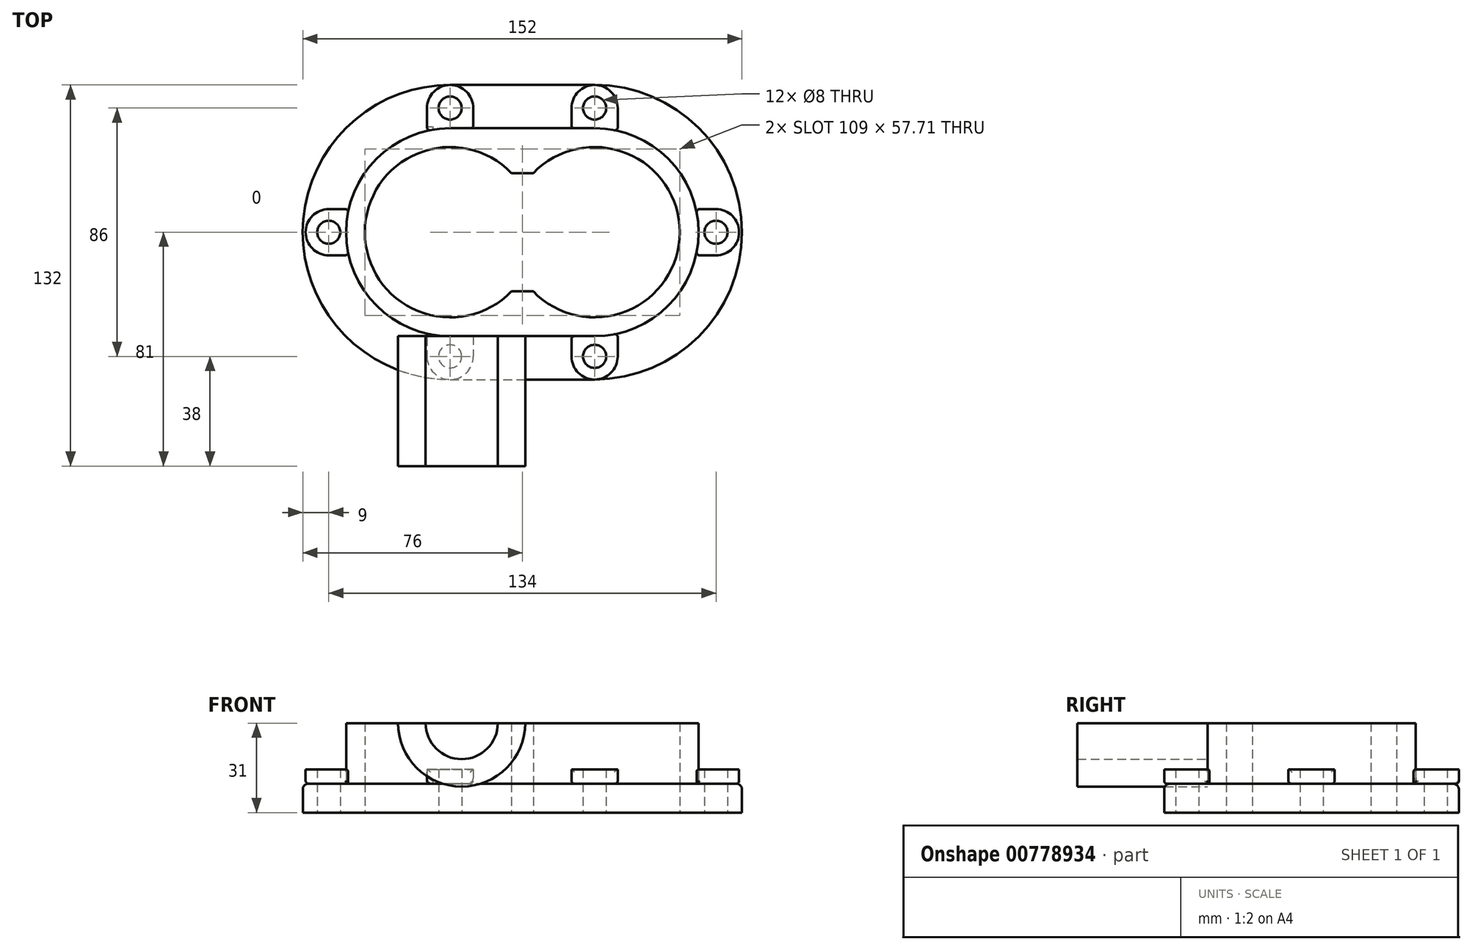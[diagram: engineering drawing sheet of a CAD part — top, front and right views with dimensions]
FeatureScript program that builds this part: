
annotation { "Feature Type Name" : "Feature", "Feature Type Description" : "" }
export const myFeature = defineFeature(function(context is Context, id is Id, definition is map)
    precondition{}
    {
        {
            var Q0;
            Q0=qCreatedBy(makeId("Top.planeOp"),FACE);
            var sketch = newSketch(context, id + "F0", { "sketchPlane" : qUnion([Q0])});
            skArc(sketch, "E0", {"start": v(-3.79, 20.5) * mm, "mid": v(-54.5, 0) * mm, "end": v(-3.79, -20.5) * mm});
            skArc(sketch, "E1", {"start": v(3.79, -20.5) * mm, "mid": v(54.5, 0) * mm, "end": v(3.79, 20.5) * mm});
            skArc(sketch, "E2", {"start": v(-25, 51) * mm, "mid": v(-76, 0) * mm, "end": v(-25, -51) * mm});
            skLineSegment(sketch, "E3", {"start": v(-25, 51) * mm, "end": v(25, 51) * mm});
            skLineSegment(sketch, "E4", {"start": v(-25, -51) * mm, "end": v(25, -51) * mm});
            skArc(sketch, "E5.trimOffspring", {"start": v(25, -51) * mm, "mid": v(76, 0) * mm, "end": v(25, 51) * mm});
            skLineSegment(sketch, "E6", {"start": v(-3.79, 20.5) * mm, "end": v(3.79, 20.5) * mm});
            skLineSegment(sketch, "E7", {"start": v(-3.79, -20.5) * mm, "end": v(3.79, -20.5) * mm});
            skCircle(sketch, "E8", {"center": v(25, 43) * mm, "radius": 4 * mm});
            skLineSegment(sketch, "E9", {"start": v(0, 0) * mm, "end": v(0, 67.16) * mm, "construction": true});
            skPoint(sketch, "E9.endSnap0", {"position": v(0, 51) * mm});
            skLineSegment(sketch, "E10", {"start": v(0, 0) * mm, "end": v(93.07, 0) * mm, "construction": true});
            skCircle(sketch, "E11.MirrorC", {"center": v(-25, 43) * mm, "radius": 4 * mm});
            skCircle(sketch, "E12.MirrorC", {"center": v(25, -43) * mm, "radius": 4 * mm});
            skCircle(sketch, "E13.MirrorC", {"center": v(-25, -43) * mm, "radius": 4 * mm});
            skCircle(sketch, "E14", {"center": v(67, 0) * mm, "radius": 4 * mm});
            skCircle(sketch, "E15.MirrorC", {"center": v(-67, 0) * mm, "radius": 4 * mm});
            skSolve(sketch);
        }
        {
            var Q0;
            Q0 = qSketchRegion(id + "F0", true);
            extrude(context, id + "F1", {"entities" : qUnion([Q0]), "depth" : 10 * mm, "offsetDistance" : 25 * mm});
        }
        {
            var Q0;
            Q0=makeQuery(id+"F1.opExtrude","CAP_FACE",FACE,{"disambiguationData":[OSD([sQuery(id+"F0.wireOp",EDGE,"E0"),sQuery(id+"F0.wireOp",EDGE,"E1"),sQuery(id+"F0.wireOp",EDGE,"E2"),sQuery(id+"F0.wireOp",EDGE,"E3"),sQuery(id+"F0.wireOp",EDGE,"E4"),sQuery(id+"F0.wireOp",EDGE,"E5.trimOffspring"),sQuery(id+"F0.wireOp",EDGE,"E6"),sQuery(id+"F0.wireOp",EDGE,"E7"),sQuery(id+"F0.wireOp",EDGE,"E8"),sQuery(id+"F0.wireOp",EDGE,"E11.MirrorC"),sQuery(id+"F0.wireOp",EDGE,"E12.MirrorC"),sQuery(id+"F0.wireOp",EDGE,"E13.MirrorC"),sQuery(id+"F0.wireOp",EDGE,"E14"),sQuery(id+"F0.wireOp",EDGE,"E15.MirrorC")])],"isStart":false});
            var sketch = newSketch(context, id + "F2", { "sketchPlane" : qUnion([Q0])});
            skArc(sketch, "E16.0", {"start": v(-3.79, 20.5) * mm, "mid": v(-54.5, 0) * mm, "end": v(-3.79, -20.5) * mm});
            skLineSegment(sketch, "E16.1", {"start": v(-3.79, 20.5) * mm, "end": v(3.79, 20.5) * mm});
            skArc(sketch, "E16.2", {"start": v(3.79, -20.5) * mm, "mid": v(54.5, 0) * mm, "end": v(3.79, 20.5) * mm});
            skLineSegment(sketch, "E16.3", {"start": v(-3.79, -20.5) * mm, "end": v(3.79, -20.5) * mm});
            skArc(sketch, "E17", {"start": v(25, -36) * mm, "mid": v(61, 0) * mm, "end": v(25, 36) * mm});
            skArc(sketch, "E18", {"start": v(-25, 36) * mm, "mid": v(-61, 0) * mm, "end": v(-25, -36) * mm});
            skLineSegment(sketch, "E19", {"start": v(-25, 36) * mm, "end": v(25, 36) * mm});
            skLineSegment(sketch, "E20", {"start": v(-25, -36) * mm, "end": v(25, -36) * mm});
            skSolve(sketch);
        }
        {
            var Q0;
            Q0 = qSketchRegion(id + "F2", true);
            extrude(context, id + "F3", {"entities" : qUnion([Q0]), "depth" : 21 * mm, "offsetDistance" : 25 * mm});
        }
        {
            var Q0;
            Q0=makeQuery(id+"F1.opExtrude","CAP_FACE",FACE,{"disambiguationData":[OSD([sQuery(id+"F0.wireOp",EDGE,"E0"),sQuery(id+"F0.wireOp",EDGE,"E1"),sQuery(id+"F0.wireOp",EDGE,"E2"),sQuery(id+"F0.wireOp",EDGE,"E3"),sQuery(id+"F0.wireOp",EDGE,"E4"),sQuery(id+"F0.wireOp",EDGE,"E5.trimOffspring"),sQuery(id+"F0.wireOp",EDGE,"E6"),sQuery(id+"F0.wireOp",EDGE,"E7"),sQuery(id+"F0.wireOp",EDGE,"E8"),sQuery(id+"F0.wireOp",EDGE,"E11.MirrorC"),sQuery(id+"F0.wireOp",EDGE,"E12.MirrorC"),sQuery(id+"F0.wireOp",EDGE,"E13.MirrorC"),sQuery(id+"F0.wireOp",EDGE,"E14"),sQuery(id+"F0.wireOp",EDGE,"E15.MirrorC")])],"isStart":false});
            var sketch = newSketch(context, id + "F4", { "sketchPlane" : qUnion([Q0])});
            skLineSegment(sketch, "E21", {"start": v(0, 0) * mm, "end": v(0, 60.03) * mm, "construction": true});
            skLineSegment(sketch, "E22", {"start": v(0, 0) * mm, "end": v(87.27, 0) * mm, "construction": true});
            skPoint(sketch, "E22.endSnap0", {"position": v(76, 0) * mm});
            skArc(sketch, "E23.0", {"start": v(60.1, -8) * mm, "mid": v(61, 0) * mm, "end": v(60.1, 8) * mm});
            skArc(sketch, "E24", {"start": v(67, -8) * mm, "mid": v(75, 0) * mm, "end": v(67, 8) * mm});
            skLineSegment(sketch, "E25", {"start": v(60.1, 8) * mm, "end": v(67, 8) * mm});
            skLineSegment(sketch, "E26", {"start": v(60.1, -8) * mm, "end": v(67, -8) * mm});
            skPoint(sketch, "E27.orphan", {"position": v(25, 36) * mm});
            skPoint(sketch, "E28.orphan", {"position": v(25, -36) * mm});
            skArc(sketch, "E29", {"start": v(33, 43) * mm, "mid": v(25, 51) * mm, "end": v(17, 43) * mm});
            skLineSegment(sketch, "E30", {"start": v(17, 36) * mm, "end": v(17, 43) * mm});
            skLineSegment(sketch, "E31", {"start": v(33, 35.1) * mm, "end": v(33, 43) * mm});
            skLineSegment(sketch, "E32", {"start": v(25, 43) * mm, "end": v(25, 19.61) * mm, "construction": true});
            skLineSegment(sketch, "E33.0", {"start": v(17, 36) * mm, "end": v(25, 36) * mm});
            skPoint(sketch, "E34.orphan", {"position": v(-25, 36) * mm});
            skArc(sketch, "E35.trimOffspring", {"start": v(33, 35.1) * mm, "mid": v(29.03, 35.77) * mm, "end": v(25, 36) * mm});
            skArc(sketch, "E36.MirrorCS", {"start": v(33, -43) * mm, "mid": v(25, -51) * mm, "end": v(17, -43) * mm});
            skLineSegment(sketch, "E37.MirrorCS", {"start": v(17, -36) * mm, "end": v(17, -43) * mm});
            skLineSegment(sketch, "E38.MirrorCS", {"start": v(33, -35.1) * mm, "end": v(33, -43) * mm});
            skArc(sketch, "E39.MirrorCS", {"start": v(33, -35.1) * mm, "mid": v(29.03, -35.77) * mm, "end": v(25, -36) * mm});
            skLineSegment(sketch, "E40.MirrorCS", {"start": v(17, -36) * mm, "end": v(25, -36) * mm});
            skLineSegment(sketch, "E41.MirrorCS", {"start": v(-17, 36) * mm, "end": v(-17, 43) * mm});
            skArc(sketch, "E42.MirrorCS", {"start": v(-33, 43) * mm, "mid": v(-25, 51) * mm, "end": v(-17, 43) * mm});
            skLineSegment(sketch, "E43.MirrorCS", {"start": v(-33, 35.1) * mm, "end": v(-33, 43) * mm});
            skArc(sketch, "E44.MirrorCS", {"start": v(-33, 35.1) * mm, "mid": v(-29.03, 35.77) * mm, "end": v(-25, 36) * mm});
            skLineSegment(sketch, "E45.MirrorCS", {"start": v(-17, 36) * mm, "end": v(-25, 36) * mm});
            skLineSegment(sketch, "E46.MirrorCS", {"start": v(-60.1, 8) * mm, "end": v(-67, 8) * mm});
            skArc(sketch, "E47.MirrorCS", {"start": v(-60.1, -8) * mm, "mid": v(-61, 0) * mm, "end": v(-60.1, 8) * mm});
            skLineSegment(sketch, "E48.MirrorCS", {"start": v(-60.1, -8) * mm, "end": v(-67, -8) * mm});
            skArc(sketch, "E49.MirrorCS", {"start": v(-67, -8) * mm, "mid": v(-75, 0) * mm, "end": v(-67, 8) * mm});
            skArc(sketch, "E50.MirrorCS", {"start": v(-33, -35.1) * mm, "mid": v(-29.03, -35.77) * mm, "end": v(-25, -36) * mm});
            skLineSegment(sketch, "E51.MirrorCS", {"start": v(-17, -36) * mm, "end": v(-25, -36) * mm});
            skLineSegment(sketch, "E52.MirrorCS", {"start": v(-17, -36) * mm, "end": v(-17, -43) * mm});
            skLineSegment(sketch, "E53.MirrorCS", {"start": v(-33, -35.1) * mm, "end": v(-33, -43) * mm});
            skArc(sketch, "E54.MirrorCS", {"start": v(-33, -43) * mm, "mid": v(-25, -51) * mm, "end": v(-17, -43) * mm});
            skCircle(sketch, "E55", {"center": v(25, 43) * mm, "radius": 4 * mm});
            skCircle(sketch, "E56", {"center": v(67, 0) * mm, "radius": 4 * mm});
            skCircle(sketch, "E57", {"center": v(25, -43) * mm, "radius": 4 * mm});
            skCircle(sketch, "E58", {"center": v(-25, -43) * mm, "radius": 4 * mm});
            skCircle(sketch, "E59", {"center": v(-25, 43) * mm, "radius": 4 * mm});
            skCircle(sketch, "E60", {"center": v(-67, 0) * mm, "radius": 4 * mm});
            skSolve(sketch);
        }
        {
            var Q0;
            Q0 = qSketchRegion(id + "F4", true);
            extrude(context, id + "F5", {"entities" : qUnion([Q0]), "depth" : 5 * mm, "offsetDistance" : 25 * mm});
        }
        {
            var Q0;
            Q0=makeQuery(id+"F5.opExtrude","CAP_EDGE",EDGE,{"disambiguationData":[OSD([sQuery(id+"F4.wireOp",EDGE,"E42.MirrorCS")])],"isStart":true});
            var Q1;
            Q1=makeQuery(id+"F1.opExtrude","CAP_EDGE",EDGE,{"disambiguationData":[OSD([sQuery(id+"F0.wireOp",EDGE,"E2")])],"isStart":false});
            fillet(context, id + "F6", {"entities" : qUnion([Q0, Q1]), "radius" : 2 * mm, "tangentPropagation" : true, "allowEdgeOverflow" : false});
        }
        {
            var Q0;
            Q0=makeQuery(id+"F3.opExtrude","CAP_EDGE",EDGE,{"disambiguationData":[OSD([sQuery(id+"F2.wireOp",EDGE,"E20")])],"isStart":true});
            fillet(context, id + "F7", {"entities" : qUnion([Q0]), "radius" : 1 * mm, "tangentPropagation" : true, "allowEdgeOverflow" : false});
        }
        {
            var Q0;
            Q0=makeQuery(id+"F3.opExtrude","SWEPT_FACE",FACE,{"disambiguationData":[OSD([sQuery(id+"F2.wireOp",EDGE,"E20")])]});
            var sketch = newSketch(context, id + "F8", { "sketchPlane" : qUnion([Q0])});
            skArc(sketch, "E61", {"start": v(-33.5, 31) * mm, "mid": v(-21, 18.5) * mm, "end": v(-8.5, 31) * mm});
            skArc(sketch, "E62", {"start": v(-43, 31) * mm, "mid": v(-21, 9) * mm, "end": v(1, 31) * mm});
            skLineSegment(sketch, "E63", {"start": v(-33.5, 31) * mm, "end": v(-43, 31) * mm});
            skLineSegment(sketch, "E64", {"start": v(-8.5, 31) * mm, "end": v(1, 31) * mm});
            skSolve(sketch);
        }
        {
            var Q0;
            Q0 = qSketchRegion(id + "F8", true);
            extrude(context, id + "F9", {"entities" : qUnion([Q0]), "depth" : 45 * mm, "offsetDistance" : 25 * mm});
        }
        {
            var Q0;
            Q0=makeQuery(id+"F3.opExtrude","SWEPT_FACE",FACE,{"disambiguationData":[OSD([sQuery(id+"F2.wireOp",EDGE,"E20")])]});
            var sketch = newSketch(context, id + "F10", { "sketchPlane" : qUnion([Q0])});
            skSolve(sketch);
        }
        {
            var Q0;
            Q0=makeQuery(id+"F5.opExtrude","CAP_EDGE",EDGE,{"disambiguationData":[OSD([sQuery(id+"F4.wireOp",EDGE,"E36.MirrorCS")])],"isStart":true});
            var Q1;
            Q1=makeQuery(id+"F5.opExtrude","SWEPT_EDGE",EDGE,{"disambiguationData":[OSD([sQuery(id+"F4.wireOp",EDGE,"E38.MirrorCS"),sQuery(id+"F4.wireOp",EDGE,"E39.MirrorCS")])]});
            var Q2;
            Q2=makeQuery(id+"F5.opExtrude","CAP_EDGE",EDGE,{"disambiguationData":[OSD([sQuery(id+"F4.wireOp",EDGE,"E39.MirrorCS")])],"isStart":false});
            var Q3;
            Q3=makeQuery(id+"F5.opExtrude","SWEPT_EDGE",EDGE,{"disambiguationData":[OSD([sQuery(id+"F4.wireOp",EDGE,"E37.MirrorCS"),sQuery(id+"F4.wireOp",EDGE,"E40.MirrorCS")])]});
            var Q4;
            Q4=makeQuery(id+"F5.opExtrude","CAP_EDGE",EDGE,{"disambiguationData":[OSD([sQuery(id+"F4.wireOp",EDGE,"E53.MirrorCS")])],"isStart":true});
            var Q5;
            Q5=makeQuery(id+"F5.opExtrude","SWEPT_EDGE",EDGE,{"disambiguationData":[OSD([sQuery(id+"F4.wireOp",EDGE,"E50.MirrorCS"),sQuery(id+"F4.wireOp",EDGE,"E53.MirrorCS")])]});
            var Q6;
            Q6=makeQuery(id+"F5.opExtrude","CAP_EDGE",EDGE,{"disambiguationData":[OSD([sQuery(id+"F4.wireOp",EDGE,"E49.MirrorCS")])],"isStart":true});
            var Q7;
            Q7=makeQuery(id+"F5.opExtrude","CAP_EDGE",EDGE,{"disambiguationData":[OSD([sQuery(id+"F4.wireOp",EDGE,"E47.MirrorCS")])],"isStart":false});
            var Q8;
            Q8=makeQuery(id+"F5.opExtrude","SWEPT_EDGE",EDGE,{"disambiguationData":[OSD([sQuery(id+"F4.wireOp",EDGE,"E46.MirrorCS"),sQuery(id+"F4.wireOp",EDGE,"E47.MirrorCS")])]});
            var Q9;
            Q9=makeQuery(id+"F5.opExtrude","SWEPT_EDGE",EDGE,{"disambiguationData":[OSD([sQuery(id+"F4.wireOp",EDGE,"E47.MirrorCS"),sQuery(id+"F4.wireOp",EDGE,"E48.MirrorCS")])]});
            var Q10;
            Q10=makeQuery(id+"F5.opExtrude","CAP_EDGE",EDGE,{"disambiguationData":[OSD([sQuery(id+"F4.wireOp",EDGE,"E45.MirrorCS")])],"isStart":false});
            var Q11;
            Q11=makeQuery(id+"F5.opExtrude","SWEPT_EDGE",EDGE,{"disambiguationData":[OSD([sQuery(id+"F4.wireOp",EDGE,"E41.MirrorCS"),sQuery(id+"F4.wireOp",EDGE,"E45.MirrorCS")])]});
            var Q12;
            Q12=makeQuery(id+"F5.opExtrude","CAP_EDGE",EDGE,{"disambiguationData":[OSD([sQuery(id+"F4.wireOp",EDGE,"E31")])],"isStart":true});
            var Q13;
            Q13=makeQuery(id+"F5.opExtrude","SWEPT_EDGE",EDGE,{"disambiguationData":[OSD([sQuery(id+"F4.wireOp",EDGE,"E31"),sQuery(id+"F4.wireOp",EDGE,"E35.trimOffspring")])]});
            var Q14;
            Q14=makeQuery(id+"F5.opExtrude","CAP_EDGE",EDGE,{"disambiguationData":[OSD([sQuery(id+"F4.wireOp",EDGE,"E35.trimOffspring")])],"isStart":false});
            var Q15;
            Q15=makeQuery(id+"F5.opExtrude","SWEPT_EDGE",EDGE,{"disambiguationData":[OSD([sQuery(id+"F4.wireOp",EDGE,"E30"),sQuery(id+"F4.wireOp",EDGE,"E33.0")])]});
            var Q16;
            Q16=makeQuery(id+"F5.opExtrude","CAP_EDGE",EDGE,{"disambiguationData":[OSD([sQuery(id+"F4.wireOp",EDGE,"E24")])],"isStart":true});
            var Q17;
            Q17=makeQuery(id+"F5.opExtrude","CAP_EDGE",EDGE,{"disambiguationData":[OSD([sQuery(id+"F4.wireOp",EDGE,"E23.0")])],"isStart":false});
            var Q18;
            Q18=makeQuery(id+"F5.opExtrude","SWEPT_EDGE",EDGE,{"disambiguationData":[OSD([sQuery(id+"F4.wireOp",EDGE,"E26"),sQuery(id+"F4.wireOp",EDGE,"E23.0")])]});
            var Q19;
            Q19=makeQuery(id+"F5.opExtrude","SWEPT_EDGE",EDGE,{"disambiguationData":[OSD([sQuery(id+"F4.wireOp",EDGE,"E25"),sQuery(id+"F4.wireOp",EDGE,"E23.0")])]});
            fillet(context, id + "F11", {"entities" : qUnion([Q0, Q1, Q2, Q3, Q4, Q5, Q6, Q7, Q8, Q9, Q10, Q11, Q12, Q13, Q14, Q15, Q16, Q17, Q18, Q19]), "radius" : 1 * mm, "tangentPropagation" : true, "allowEdgeOverflow" : false});
        }
    });
